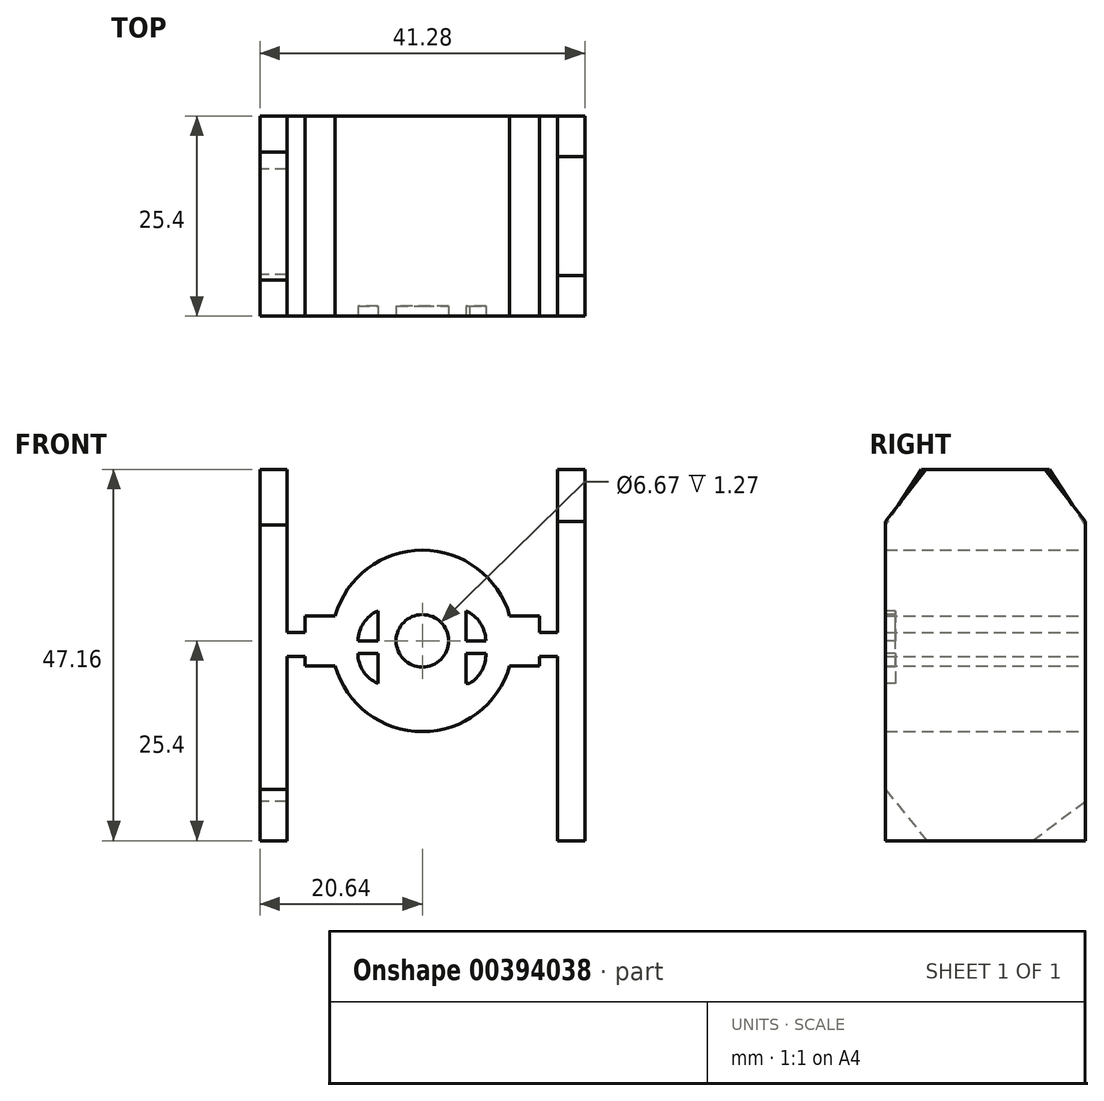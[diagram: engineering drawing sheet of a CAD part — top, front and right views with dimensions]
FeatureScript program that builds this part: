
annotation { "Feature Type Name" : "Feature", "Feature Type Description" : "" }
export const myFeature = defineFeature(function(context is Context, id is Id, definition is map)
    precondition{}
    {
        {
            var Q0;
            Q0=qCreatedBy(makeId("Front.planeOp"),FACE);
            var sketch = newSketch(context, id + "F0", { "sketchPlane" : qUnion([Q0])});
            skLineSegment(sketch, "E0", {"start": v(0, 0) * mm, "end": v(50.8, 0) * mm});
            skLineSegment(sketch, "E1", {"start": v(50.8, 0) * mm, "end": v(50.8, 50.8) * mm});
            skLineSegment(sketch, "E2", {"start": v(50.8, 50.8) * mm, "end": v(0, 50.8) * mm});
            skLineSegment(sketch, "E3", {"start": v(0, 50.8) * mm, "end": v(0, 0) * mm});
            skCircle(sketch, "E4", {"center": v(25.4, 25.4) * mm, "radius": 11.53 * mm});
            skPoint(sketch, "E4.centerSnap0", {"position": v(50.8, 25.4) * mm});
            skPoint(sketch, "E4.centerSnap1", {"position": v(25.4, 0) * mm});
            skLineSegment(sketch, "E5", {"start": v(0, 0) * mm, "end": v(4.76, 0) * mm});
            skLineSegment(sketch, "E6", {"start": v(14.31, 28.58) * mm, "end": v(10.5, 28.58) * mm});
            skLineSegment(sketch, "E7", {"start": v(10.5, 28.58) * mm, "end": v(10.5, 22.23) * mm});
            skLineSegment(sketch, "E8", {"start": v(10.5, 22.23) * mm, "end": v(14.31, 22.23) * mm});
            skLineSegment(sketch, "E9", {"start": v(36.49, 22.22) * mm, "end": v(40.3, 22.22) * mm});
            skLineSegment(sketch, "E10", {"start": v(40.3, 22.22) * mm, "end": v(40.3, 28.57) * mm});
            skLineSegment(sketch, "E11", {"start": v(40.3, 28.57) * mm, "end": v(36.49, 28.57) * mm});
            skLineSegment(sketch, "E12", {"start": v(10.5, 26.5) * mm, "end": v(8.22, 26.5) * mm});
            skLineSegment(sketch, "E13", {"start": v(8.22, 26.5) * mm, "end": v(8.22, 23.44) * mm});
            skLineSegment(sketch, "E14", {"start": v(8.22, 23.44) * mm, "end": v(10.5, 23.44) * mm});
            skLineSegment(sketch, "E15", {"start": v(40.3, 26.5) * mm, "end": v(42.58, 26.5) * mm});
            skLineSegment(sketch, "E16", {"start": v(42.58, 26.5) * mm, "end": v(42.58, 23.44) * mm});
            skLineSegment(sketch, "E17", {"start": v(42.58, 23.44) * mm, "end": v(40.3, 23.44) * mm});
            skLineSegment(sketch, "E18", {"start": v(8.22, 26.5) * mm, "end": v(8.22, 47.16) * mm});
            skLineSegment(sketch, "E19", {"start": v(8.22, 47.16) * mm, "end": v(4.76, 47.16) * mm});
            skLineSegment(sketch, "E20", {"start": v(4.76, 47.16) * mm, "end": v(4.76, 0) * mm});
            skLineSegment(sketch, "E21", {"start": v(8.22, 0) * mm, "end": v(8.22, 23.44) * mm});
            skLineSegment(sketch, "E22", {"start": v(42.58, 26.5) * mm, "end": v(42.58, 47.16) * mm});
            skLineSegment(sketch, "E23", {"start": v(42.58, 47.16) * mm, "end": v(46.04, 47.16) * mm});
            skLineSegment(sketch, "E24", {"start": v(46.04, 47.16) * mm, "end": v(46.04, 0) * mm});
            skLineSegment(sketch, "E25", {"start": v(46.04, 0) * mm, "end": v(42.58, 0) * mm});
            skLineSegment(sketch, "E26", {"start": v(42.58, 0) * mm, "end": v(42.58, 23.44) * mm});
            skSolve(sketch);
        }
        {
            var Q0;
            Q0=makeQuery(id+"F0.imprint","IMPRINT",FACE,{"disambiguationData":[TD([[makeQuery(id+"F0.imprint","IMPRINT",EDGE,{"derivedFrom":sQuery(id+"F0.wireOp",EDGE,"E16")}),1.0]])]});
            var Q1;
            Q1=makeQuery(id+"F0.imprint","IMPRINT",FACE,{"disambiguationData":[TD([[makeQuery(id+"F0.imprint","IMPRINT",EDGE,{"derivedFrom":sQuery(id+"F0.wireOp",EDGE,"E13")}),-1.0]])]});
            var Q2;
            {var subQ0=sQuery(id+"F0.wireOp",EDGE,"E4");var subQ1=makeQuery(id+"F0.imprint","INTERSECT",VERTEX,{"derivedFrom":[subQ0,sQuery(id+"F0.wireOp",EDGE,"E6")]});Q2=makeQuery(id+"F0.imprint","IMPRINT",FACE,{"disambiguationData":[TD([[makeQuery(id+"F0.imprint","IMPRINT",EDGE,{"disambiguationData":[TD([[subQ1,1.0]])],"derivedFrom":subQ0}),1.0]])]});}
            var Q3;
            {var subQ0=sQuery(id+"F0.wireOp",EDGE,"E12");Q3=makeQuery(id+"F0.imprint","IMPRINT",FACE,{"disambiguationData":[TD([[makeQuery(id+"F0.imprint","IMPRINT",EDGE,{"derivedFrom":subQ0}),1.0]])]});}
            var Q4;
            {var subQ3=sQuery(id+"F0.wireOp",EDGE,"E6");Q4=makeQuery(id+"F0.imprint","IMPRINT",FACE,{"disambiguationData":[TD([[makeQuery(id+"F0.imprint","IMPRINT",EDGE,{"derivedFrom":subQ3}),1.0]])]});}
            var Q5;
            {var subQ3=sQuery(id+"F0.wireOp",EDGE,"E9");Q5=makeQuery(id+"F0.imprint","IMPRINT",FACE,{"disambiguationData":[TD([[makeQuery(id+"F0.imprint","IMPRINT",EDGE,{"derivedFrom":subQ3}),1.0]])]});}
            var Q6;
            {var subQ0=sQuery(id+"F0.wireOp",EDGE,"E15");Q6=makeQuery(id+"F0.imprint","IMPRINT",FACE,{"disambiguationData":[TD([[makeQuery(id+"F0.imprint","IMPRINT",EDGE,{"derivedFrom":subQ0}),-1.0]])]});}
            extrude(context, id + "F1", {"entities" : qUnion([Q0, Q1, Q2, Q3, Q4, Q5, Q6]), "depth" : 25.4 * mm});
        }
        {
            var Q0;
            Q0=makeQuery(id+"F1.opExtrude","SWEPT_FACE",FACE,{"disambiguationData":[OSD([sQuery(id+"F0.wireOp",EDGE,"E24")])]});
            var sketch = newSketch(context, id + "F2", { "sketchPlane" : qUnion([Q0])});
            skLineSegment(sketch, "E27", {"start": v(-25.4, 40.55) * mm, "end": v(-20.24, 47.16) * mm});
            skLineSegment(sketch, "E28", {"start": v(-20.24, 47.16) * mm, "end": v(-5.16, 47.16) * mm});
            skLineSegment(sketch, "E29", {"start": v(-5.16, 47.16) * mm, "end": v(0, 40.55) * mm});
            skLineSegment(sketch, "E30", {"start": v(0, 40.55) * mm, "end": v(0, 7.41) * mm});
            skLineSegment(sketch, "E31", {"start": v(0, 7.41) * mm, "end": v(-3.92, 0) * mm});
            skLineSegment(sketch, "E32", {"start": v(-3.92, 0) * mm, "end": v(-20.24, 0) * mm});
            skLineSegment(sketch, "E33", {"start": v(-20.24, 0) * mm, "end": v(-25.4, 6.6) * mm});
            skLineSegment(sketch, "E34", {"start": v(-25.4, 6.6) * mm, "end": v(-25.4, 40.55) * mm});
            skCircle(sketch, "E35", {"center": v(-12.08, 23.98) * mm, "radius": 3.45 * mm});
            skPoint(sketch, "E35.centerSnap0", {"position": v(0, 23.98) * mm});
            skPoint(sketch, "E35.centerSnap1", {"position": v(-12.08, 0) * mm});
            skLineSegment(sketch, "E36", {"start": v(-23.36, 43.16) * mm, "end": v(-14.4, 26.53) * mm});
            skLineSegment(sketch, "E37", {"start": v(-22.17, 44.68) * mm, "end": v(-12.84, 27.35) * mm});
            skLineSegment(sketch, "E38", {"start": v(-1.73, 42.76) * mm, "end": v(-9.68, 26.47) * mm});
            skLineSegment(sketch, "E39", {"start": v(-2.58, 43.85) * mm, "end": v(-11.05, 27.28) * mm});
            skLineSegment(sketch, "E40", {"start": v(-22.43, 2.8) * mm, "end": v(-12.55, 20.56) * mm});
            skLineSegment(sketch, "E41", {"start": v(-14.17, 21.24) * mm, "end": v(-23.73, 4.47) * mm});
            skLineSegment(sketch, "E42", {"start": v(-23.73, 4.47) * mm, "end": v(-22.43, 2.8) * mm});
            skLineSegment(sketch, "E43", {"start": v(-9.62, 21.55) * mm, "end": v(-1, 5.53) * mm});
            skLineSegment(sketch, "E44", {"start": v(-1, 5.53) * mm, "end": v(-1.96, 3.7) * mm});
            skLineSegment(sketch, "E45", {"start": v(-1.96, 3.7) * mm, "end": v(-11.1, 20.67) * mm});
            skSolve(sketch);
        }
        {
            var Q0;
            {var subQ4=sQuery(id+"F2.wireOp",EDGE,"E27");var subQ7=makeQuery(id+"F2.imprint","INTERSECT",VERTEX,{"derivedFrom":[subQ4,sQuery(id+"F2.wireOp",EDGE,"E36")]});Q0=makeQuery(id+"F2.imprint","IMPRINT",FACE,{"disambiguationData":[TD([[makeQuery(id+"F2.imprint","IMPRINT",EDGE,{"disambiguationData":[TD([[subQ7,-1.0]])],"derivedFrom":subQ4}),1.0]])]});}
            var Q1;
            {var subQ4=sQuery(id+"F2.wireOp",EDGE,"E29");var subQ7=makeQuery(id+"F2.imprint","INTERSECT",VERTEX,{"derivedFrom":[subQ4,sQuery(id+"F2.wireOp",EDGE,"E38")]});Q1=makeQuery(id+"F2.imprint","IMPRINT",FACE,{"disambiguationData":[TD([[makeQuery(id+"F2.imprint","IMPRINT",EDGE,{"disambiguationData":[TD([[subQ7,1.0]])],"derivedFrom":subQ4}),1.0]])]});}
            var Q2;
            {var subQ0=sQuery(id+"F2.wireOp",EDGE,"E44");Q2=makeQuery(id+"F2.imprint","IMPRINT",FACE,{"disambiguationData":[TD([[makeQuery(id+"F2.imprint","IMPRINT",EDGE,{"derivedFrom":subQ0}),1.0]])]});}
            var Q3;
            {var subQ6=sQuery(id+"F2.wireOp",EDGE,"E42");Q3=makeQuery(id+"F2.imprint","IMPRINT",FACE,{"disambiguationData":[TD([[makeQuery(id+"F2.imprint","IMPRINT",EDGE,{"derivedFrom":subQ6}),-1.0]])]});}
            extrude(context, id + "F3", {"entities" : qUnion([Q0, Q1, Q2, Q3]), "operationType" : NewBodyOperationType.REMOVE, "oppositeDirection" : true, "depth" : 12.7 * mm});
        }
        {
            var Q0;
            Q0=makeQuery(id+"F1.opExtrude","SWEPT_FACE",FACE,{"disambiguationData":[OSD([sQuery(id+"F0.wireOp",EDGE,"E20")])]});
            var sketch = newSketch(context, id + "F4", { "sketchPlane" : qUnion([Q0])});
            skLineSegment(sketch, "E46", {"start": v(0, 40.14) * mm, "end": v(4.6, 47.16) * mm});
            skLineSegment(sketch, "E47", {"start": v(4.6, 47.16) * mm, "end": v(20.85, 47.16) * mm});
            skLineSegment(sketch, "E48", {"start": v(20.85, 47.16) * mm, "end": v(25.4, 40.12) * mm});
            skLineSegment(sketch, "E49", {"start": v(25.4, 40.12) * mm, "end": v(25.4, 6.51) * mm});
            skLineSegment(sketch, "E50", {"start": v(25.4, 6.51) * mm, "end": v(20.12, 0) * mm});
            skLineSegment(sketch, "E51", {"start": v(20.12, 0) * mm, "end": v(6.72, 0) * mm});
            skLineSegment(sketch, "E52", {"start": v(6.72, 0) * mm, "end": v(0, 5.01) * mm});
            skLineSegment(sketch, "E53", {"start": v(0, 5.01) * mm, "end": v(0, 40.14) * mm});
            skSolve(sketch);
        }
        {
            var Q0;
            {var subQ0=sQuery(id+"F4.wireOp",EDGE,"E46");Q0=makeQuery(id+"F4.imprint","IMPRINT",FACE,{"disambiguationData":[TD([[makeQuery(id+"F4.imprint","IMPRINT",EDGE,{"derivedFrom":subQ0}),1.0]])]});}
            var Q1;
            {var subQ0=sQuery(id+"F4.wireOp",EDGE,"E48");Q1=makeQuery(id+"F4.imprint","IMPRINT",FACE,{"disambiguationData":[TD([[makeQuery(id+"F4.imprint","IMPRINT",EDGE,{"derivedFrom":subQ0}),1.0]])]});}
            var Q2;
            {var subQ0=sQuery(id+"F4.wireOp",EDGE,"E50");Q2=makeQuery(id+"F4.imprint","IMPRINT",FACE,{"disambiguationData":[TD([[makeQuery(id+"F4.imprint","IMPRINT",EDGE,{"derivedFrom":subQ0}),1.0]])]});}
            var Q3;
            {var subQ0=sQuery(id+"F4.wireOp",EDGE,"E52");Q3=makeQuery(id+"F4.imprint","IMPRINT",FACE,{"disambiguationData":[TD([[makeQuery(id+"F4.imprint","IMPRINT",EDGE,{"derivedFrom":subQ0}),1.0]])]});}
            extrude(context, id + "F5", {"entities" : qUnion([Q0, Q1, Q2, Q3]), "operationType" : NewBodyOperationType.REMOVE, "oppositeDirection" : true, "depth" : 12.7 * mm});
        }
        {
            var Q0;
            Q0=makeQuery(id+"F1.opExtrude","CAP_FACE",FACE,{"disambiguationData":[OSD([sQuery(id+"F0.wireOp",EDGE,"E0"),sQuery(id+"F0.wireOp",EDGE,"E4"),sQuery(id+"F0.wireOp",EDGE,"E6"),sQuery(id+"F0.wireOp",EDGE,"E7"),sQuery(id+"F0.wireOp",EDGE,"E8"),sQuery(id+"F0.wireOp",EDGE,"E9"),sQuery(id+"F0.wireOp",EDGE,"E10"),sQuery(id+"F0.wireOp",EDGE,"E11"),sQuery(id+"F0.wireOp",EDGE,"E12"),sQuery(id+"F0.wireOp",EDGE,"E14"),sQuery(id+"F0.wireOp",EDGE,"E15"),sQuery(id+"F0.wireOp",EDGE,"E17"),sQuery(id+"F0.wireOp",EDGE,"E18"),sQuery(id+"F0.wireOp",EDGE,"E19"),sQuery(id+"F0.wireOp",EDGE,"E20"),sQuery(id+"F0.wireOp",EDGE,"E21"),sQuery(id+"F0.wireOp",EDGE,"E22"),sQuery(id+"F0.wireOp",EDGE,"E23"),sQuery(id+"F0.wireOp",EDGE,"E24"),sQuery(id+"F0.wireOp",EDGE,"E25"),sQuery(id+"F0.wireOp",EDGE,"E26")])],"isStart":false});
            var sketch = newSketch(context, id + "F6", { "sketchPlane" : qUnion([Q0])});
            skCircle(sketch, "E54", {"center": v(25.4, 25.4) * mm, "radius": 3.34 * mm});
            skLineSegment(sketch, "E55", {"start": v(17.2, 25.4) * mm, "end": v(19.75, 25.4) * mm});
            skLineSegment(sketch, "E56", {"start": v(19.75, 25.4) * mm, "end": v(19.75, 29.21) * mm});
            skLineSegment(sketch, "E57", {"start": v(30.9, 25.4) * mm, "end": v(33.45, 25.4) * mm});
            skLineSegment(sketch, "E58", {"start": v(33.45, 25.4) * mm, "end": v(30.9, 25.4) * mm});
            skLineSegment(sketch, "E59", {"start": v(30.9, 29.21) * mm, "end": v(30.9, 25.4) * mm});
            skLineSegment(sketch, "E60", {"start": v(19.75, 23.8) * mm, "end": v(17.2, 23.8) * mm});
            skLineSegment(sketch, "E61", {"start": v(17.2, 23.8) * mm, "end": v(19.75, 23.8) * mm});
            skLineSegment(sketch, "E62", {"start": v(19.75, 23.8) * mm, "end": v(19.75, 20) * mm});
            skLineSegment(sketch, "E63", {"start": v(30.9, 23.8) * mm, "end": v(33.45, 23.8) * mm});
            skLineSegment(sketch, "E64", {"start": v(33.45, 23.8) * mm, "end": v(30.9, 23.8) * mm});
            skLineSegment(sketch, "E65", {"start": v(30.9, 20) * mm, "end": v(30.9, 23.8) * mm});
            skArc(sketch, "E66", {"start": v(19.75, 29.21) * mm, "mid": v(17.93, 27.67) * mm, "end": v(17.2, 25.4) * mm});
            skArc(sketch, "E67", {"start": v(33.45, 25.4) * mm, "mid": v(32.74, 27.68) * mm, "end": v(30.9, 29.21) * mm});
            skArc(sketch, "E68", {"start": v(31.4, 20) * mm, "mid": v(32.96, 21.62) * mm, "end": v(33.45, 23.8) * mm});
            skArc(sketch, "E69", {"start": v(17.2, 23.8) * mm, "mid": v(17.9, 21.52) * mm, "end": v(19.75, 20) * mm});
            skLineSegment(sketch, "E70", {"start": v(30.9, 20) * mm, "end": v(31.4, 20) * mm});
            skSolve(sketch);
        }
        {
            var Q0;
            Q0 = qSketchRegion(id + "F6", true);
            extrude(context, id + "F7", {"entities" : qUnion([Q0]), "operationType" : NewBodyOperationType.REMOVE, "oppositeDirection" : true, "depth" : 1.27 * mm});
        }
    });
